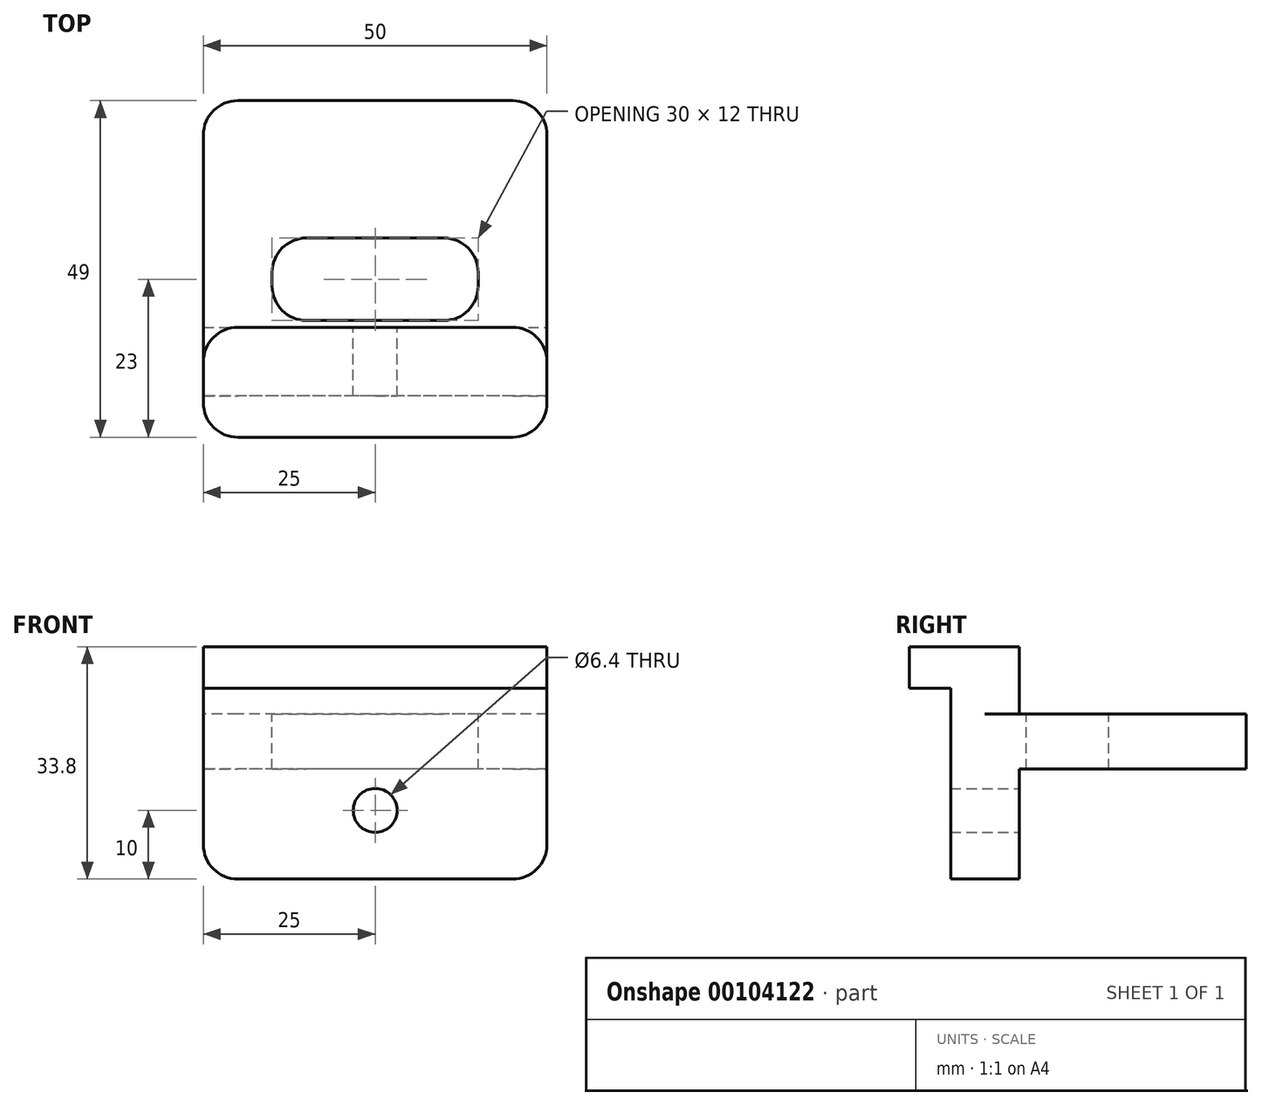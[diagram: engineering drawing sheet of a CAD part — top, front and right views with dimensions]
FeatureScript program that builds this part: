
annotation { "Feature Type Name" : "Feature", "Feature Type Description" : "" }
export const myFeature = defineFeature(function(context is Context, id is Id, definition is map)
    precondition{}
    {
        {
            var Q0;
            Q0=qCreatedBy(makeId("Right.planeOp"),FACE);
            var sketch = newSketch(context, id + "F0", { "sketchPlane" : qUnion([Q0])});
            skLineSegment(sketch, "E0", {"start": v(0, 0) * mm, "end": v(0, -8) * mm});
            skLineSegment(sketch, "E1", {"start": v(0, -8) * mm, "end": v(-33, -8) * mm});
            skLineSegment(sketch, "E2", {"start": v(-43, -24) * mm, "end": v(-33, -24) * mm});
            skLineSegment(sketch, "E3", {"start": v(-33, -24) * mm, "end": v(-33, -8) * mm});
            skLineSegment(sketch, "E4", {"start": v(-43, -24) * mm, "end": v(-43, 3.8) * mm});
            skLineSegment(sketch, "E5", {"start": v(-43, 3.8) * mm, "end": v(-49, 3.8) * mm});
            skLineSegment(sketch, "E6", {"start": v(-49, 3.8) * mm, "end": v(-49, 9.8) * mm});
            skLineSegment(sketch, "E7", {"start": v(-49, 9.8) * mm, "end": v(-33, 9.8) * mm});
            skLineSegment(sketch, "E8", {"start": v(-33, 9.8) * mm, "end": v(-33, 0) * mm});
            skLineSegment(sketch, "E9", {"start": v(-33, 0) * mm, "end": v(0, 0) * mm});
            skSolve(sketch);
        }
        {
            var Q0;
            Q0=makeQuery(id+"F0.imprint","IMPRINT",FACE,{"disambiguationData":[TD([[makeQuery(id+"F0.imprint","IMPRINT",EDGE,{"derivedFrom":sQuery(id+"F0.wireOp",EDGE,"E0")}),-1.0]])]});
            extrude(context, id + "F1", {"entities" : qUnion([Q0]), "depth" : 50 * mm});
        }
        {
            var Q0;
            Q0=makeQuery(id+"F1.opExtrude","SWEPT_FACE",FACE,{"disambiguationData":[OSD([sQuery(id+"F0.wireOp",EDGE,"E9")])]});
            var sketch = newSketch(context, id + "F2", { "sketchPlane" : qUnion([Q0])});
            skLineSegment(sketch, "E10.0", {"start": v(50, -38) * mm, "end": v(50, -5) * mm});
            skLineSegment(sketch, "E10.1", {"start": v(45, 0) * mm, "end": v(5, 0) * mm});
            skLineSegment(sketch, "E10.2", {"start": v(0, -38) * mm, "end": v(0, -5) * mm});
            skCircle(sketch, "E11", {"center": v(40.95, -9.76) * mm, "radius": 3 * mm});
            skCircle(sketch, "E12", {"center": v(8.18, -8.62) * mm, "radius": 3 * mm});
            skCircle(sketch, "E13", {"center": v(24.67, -9.86) * mm, "radius": 2.5 * mm});
            skLineSegment(sketch, "E14.0", {"start": v(45, -33) * mm, "end": v(5, -33) * mm});
            skLineSegment(sketch, "E15", {"start": v(40, -32) * mm, "end": v(10, -32) * mm});
            skLineSegment(sketch, "E16", {"start": v(10, -32) * mm, "end": v(10, -20) * mm});
            skLineSegment(sketch, "E17", {"start": v(10, -20) * mm, "end": v(40, -20) * mm});
            skLineSegment(sketch, "E18", {"start": v(40, -20) * mm, "end": v(40, -32) * mm});
            skSolve(sketch);
        }
        {
            var Q0;
            Q0=makeQuery(id+"F1.opExtrude","SWEPT_FACE",FACE,{"disambiguationData":[OSD([sQuery(id+"F0.wireOp",EDGE,"E3")])]});
            var sketch = newSketch(context, id + "F3", { "sketchPlane" : qUnion([Q0])});
            skLineSegment(sketch, "E19.0", {"start": v(-45, 0) * mm, "end": v(-5, 0) * mm});
            skCircle(sketch, "E20", {"center": v(-25, -14) * mm, "radius": 3.2 * mm});
            skPoint(sketch, "E20.centerSnap0", {"position": v(-25, -8) * mm});
            skSolve(sketch);
        }
        {
            var Q0;
            Q0=makeQuery(id+"F3.imprint","IMPRINT",FACE,{"disambiguationData":[TD([[makeQuery(id+"F3.imprint","IMPRINT",EDGE,{"derivedFrom":sQuery(id+"F3.wireOp",EDGE,"E20")}),1.0]])]});
            extrude(context, id + "F4", {"entities" : qUnion([Q0]), "operationType" : NewBodyOperationType.REMOVE, "endBound" : BoundingType.THROUGH_ALL, "oppositeDirection" : true, "depth" : 25 * mm});
        }
        {
            var Q0;
            Q0=makeQuery(id+"F2.imprint","IMPRINT",FACE,{"disambiguationData":[TD([[makeQuery(id+"F2.imprint","IMPRINT",EDGE,{"derivedFrom":sQuery(id+"F2.wireOp",EDGE,"E15")}),-1.0]])]});
            extrude(context, id + "F5", {"entities" : qUnion([Q0]), "operationType" : NewBodyOperationType.REMOVE, "endBound" : BoundingType.THROUGH_ALL, "oppositeDirection" : true, "depth" : 25 * mm});
        }
        {
            var Q0;
            Q0=makeQuery(id+"F1.opExtrude","CAP_EDGE",EDGE,{"disambiguationData":[OSD([sQuery(id+"F0.wireOp",EDGE,"E0")])],"isStart":false});
            var Q1;
            Q1=makeQuery(id+"F1.opExtrude","CAP_EDGE",EDGE,{"disambiguationData":[OSD([sQuery(id+"F0.wireOp",EDGE,"E0")])],"isStart":true});
            var Q2;
            Q2=makeQuery(id+"F1.opExtrude","CAP_EDGE",EDGE,{"disambiguationData":[OSD([sQuery(id+"F0.wireOp",EDGE,"E8")])],"isStart":false});
            var Q3;
            Q3=makeQuery(id+"F1.opExtrude","CAP_EDGE",EDGE,{"disambiguationData":[OSD([sQuery(id+"F0.wireOp",EDGE,"E8")])],"isStart":true});
            var Q4;
            Q4=makeQuery(id+"F1.opExtrude","CAP_EDGE",EDGE,{"disambiguationData":[OSD([sQuery(id+"F0.wireOp",EDGE,"E6")])],"isStart":false});
            var Q5;
            Q5=makeQuery(id+"F1.opExtrude","CAP_EDGE",EDGE,{"disambiguationData":[OSD([sQuery(id+"F0.wireOp",EDGE,"E6")])],"isStart":true});
            var Q6;
            Q6=makeQuery(id+"F1.opExtrude","CAP_EDGE",EDGE,{"disambiguationData":[OSD([sQuery(id+"F0.wireOp",EDGE,"E2")])],"isStart":false});
            var Q7;
            Q7=makeQuery(id+"F1.opExtrude","CAP_EDGE",EDGE,{"disambiguationData":[OSD([sQuery(id+"F0.wireOp",EDGE,"E2")])],"isStart":true});
            var Q8;
            Q8=makeQuery(id+"F5.boolean.opBoolean","COPY",EDGE,{"derivedFrom":makeQuery(id+"F5.opExtrude","SWEPT_EDGE",EDGE,{"disambiguationData":[OSD([sQuery(id+"F2.wireOp",EDGE,"E15"),sQuery(id+"F2.wireOp",EDGE,"E16")])]})});
            var Q9;
            Q9=makeQuery(id+"F5.boolean.opBoolean","COPY",EDGE,{"derivedFrom":makeQuery(id+"F5.opExtrude","SWEPT_EDGE",EDGE,{"disambiguationData":[OSD([sQuery(id+"F2.wireOp",EDGE,"E15"),sQuery(id+"F2.wireOp",EDGE,"E18")])]})});
            var Q10;
            Q10=makeQuery(id+"F5.boolean.opBoolean","COPY",EDGE,{"derivedFrom":makeQuery(id+"F5.opExtrude","SWEPT_EDGE",EDGE,{"disambiguationData":[OSD([sQuery(id+"F2.wireOp",EDGE,"E17"),sQuery(id+"F2.wireOp",EDGE,"E18")])]})});
            var Q11;
            Q11=makeQuery(id+"F5.boolean.opBoolean","COPY",EDGE,{"derivedFrom":makeQuery(id+"F5.opExtrude","SWEPT_EDGE",EDGE,{"disambiguationData":[OSD([sQuery(id+"F2.wireOp",EDGE,"E16"),sQuery(id+"F2.wireOp",EDGE,"E17")])]})});
            fillet(context, id + "F6", {"entities" : qUnion([Q0, Q1, Q2, Q3, Q4, Q5, Q6, Q7, Q8, Q9, Q10, Q11]), "radius" : 5 * mm, "tangentPropagation" : true, "allowEdgeOverflow" : false});
        }
    });
